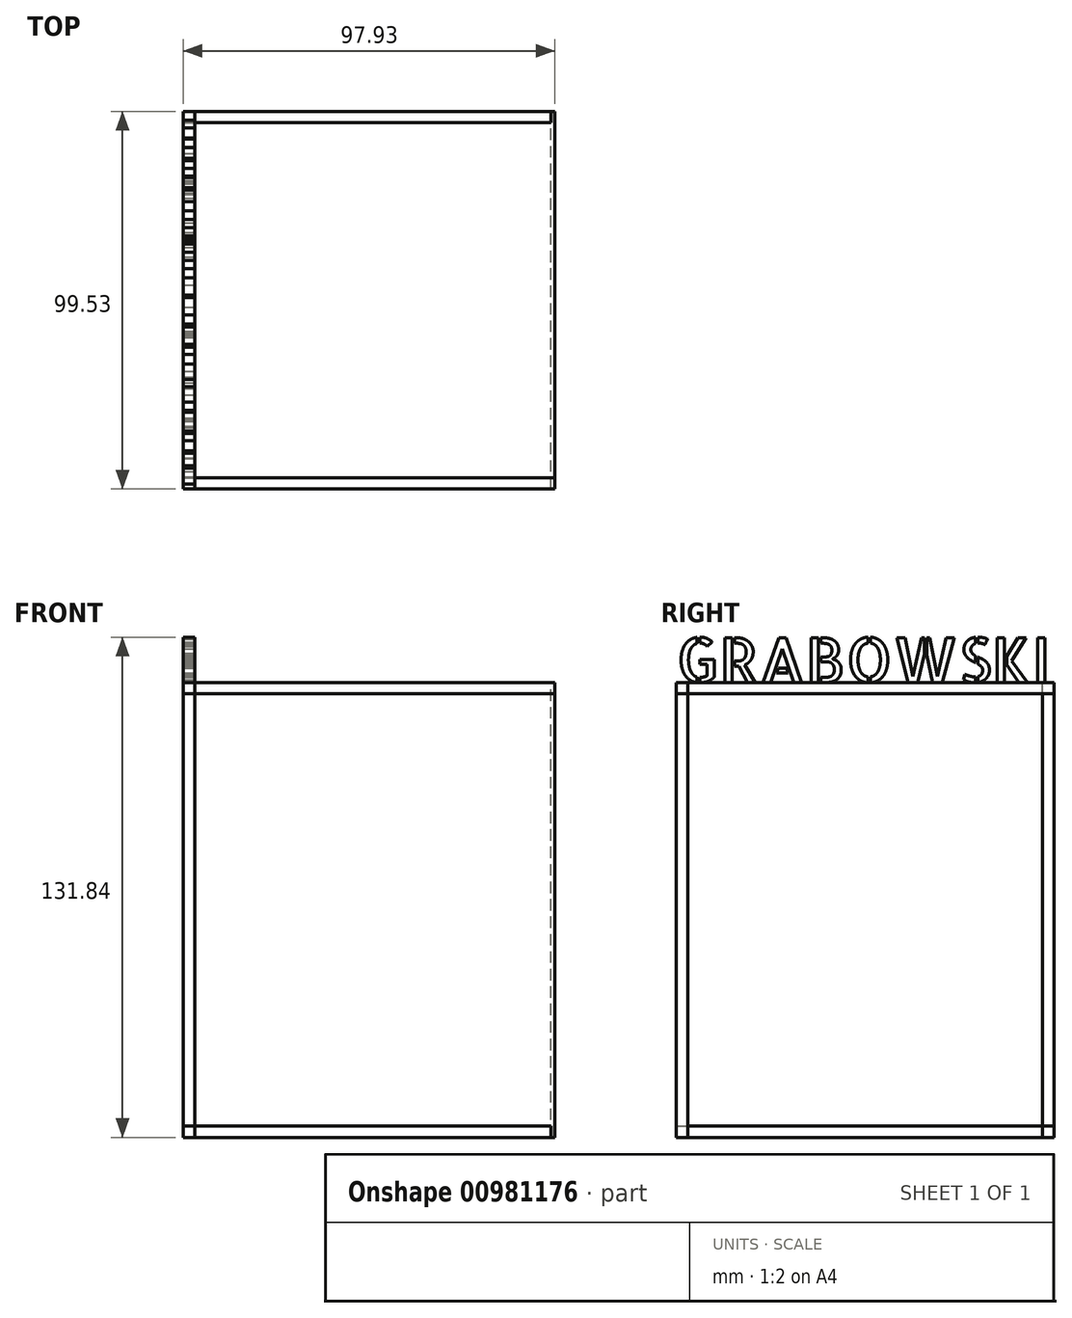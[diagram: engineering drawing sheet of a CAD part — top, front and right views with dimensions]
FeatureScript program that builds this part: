
annotation { "Feature Type Name" : "Feature", "Feature Type Description" : "" }
export const myFeature = defineFeature(function(context is Context, id is Id, definition is map)
    precondition{}
    {
        {
            var Q0;
            Q0=qCreatedBy(makeId("Front.planeOp"),FACE);
            var sketch = newSketch(context, id + "F0", { "sketchPlane" : qUnion([Q0])});
            skLineSegment(sketch, "E0.bottom", {"start": v(-41.77, 46.94) * mm, "end": v(56.16, 46.94) * mm});
            skLineSegment(sketch, "E0.top", {"start": v(-41.77, -72.94) * mm, "end": v(56.16, -72.94) * mm});
            skLineSegment(sketch, "E0.left", {"start": v(-41.77, 46.94) * mm, "end": v(-41.77, -72.94) * mm});
            skLineSegment(sketch, "E0.right", {"start": v(56.16, 46.94) * mm, "end": v(56.16, -72.94) * mm});
            skSolve(sketch);
        }
        {
            var Q0;
            Q0 = qSketchRegion(id + "F0", true);
            extrude(context, id + "F1", {"entities" : qUnion([Q0]), "depth" : 3 * mm, "offsetDistance" : 25 * mm});
        }
        {
            var Q0;
            Q0=makeQuery(id+"F1.opExtrude","SWEPT_FACE",FACE,{"disambiguationData":[OSD([sQuery(id+"F0.wireOp",EDGE,"E0.left")])]});
            var sketch = newSketch(context, id + "F2", { "sketchPlane" : qUnion([Q0])});
            skLineSegment(sketch, "E1.bottom", {"start": v(3, 46.94) * mm, "end": v(-96.53, 46.94) * mm});
            skLineSegment(sketch, "E1.top", {"start": v(3, -72.94) * mm, "end": v(-96.53, -72.94) * mm});
            skLineSegment(sketch, "E1.left", {"start": v(3, 46.94) * mm, "end": v(3, -72.94) * mm});
            skLineSegment(sketch, "E1.right", {"start": v(-96.53, 46.94) * mm, "end": v(-96.53, -72.94) * mm});
            skSolve(sketch);
        }
        {
            var Q0;
            {var subQ1=sQuery(id+"F0.wireOp",EDGE,"E0.left");var subQ2=makeQuery(id+"F1.opExtrude","CAP_EDGE",EDGE,{"disambiguationData":[OSD([subQ1])],"isStart":true});Q0=makeQuery(id+"F2.imprint","IMPRINT",FACE,{"disambiguationData":[TD([[makeQuery(id+"F2.imprint","IMPRINT",EDGE,{"derivedFrom":subQ2}),1.0]])]});}
            extrude(context, id + "F3", {"entities" : qUnion([Q0]), "operationType" : NewBodyOperationType.ADD, "oppositeDirection" : true, "depth" : 3 * mm, "offsetDistance" : 25 * mm});
        }
        {
            var Q0;
            Q0 = qSketchRegion(id + "F2", true);
            extrude(context, id + "F4", {"entities" : qUnion([Q0]), "oppositeDirection" : true, "depth" : 3 * mm, "offsetDistance" : 25 * mm});
        }
        {
            var Q0;
            Q0=makeQuery(id+"F4.opExtrude","SWEPT_FACE",FACE,{"disambiguationData":[OSD([sQuery(id+"F2.wireOp",EDGE,"E1.right")])]});
            var sketch = newSketch(context, id + "F5", { "sketchPlane" : qUnion([Q0])});
            skLineSegment(sketch, "E2.bottom", {"start": v(41.77, -72.94) * mm, "end": v(-55.1, -72.94) * mm});
            skLineSegment(sketch, "E2.top", {"start": v(41.77, 46.94) * mm, "end": v(-55.1, 46.94) * mm});
            skLineSegment(sketch, "E2.left", {"start": v(41.77, -72.94) * mm, "end": v(41.77, 46.94) * mm});
            skLineSegment(sketch, "E2.right", {"start": v(-55.1, -72.94) * mm, "end": v(-55.1, 46.94) * mm});
            skPoint(sketch, "E3.0", {"position": v(-56.16, -72.94) * mm});
            skSolve(sketch);
        }
        {
            var Q0;
            Q0 = qSketchRegion(id + "F5", true);
            extrude(context, id + "F6", {"entities" : qUnion([Q0]), "oppositeDirection" : true, "depth" : 3 * mm, "offsetDistance" : 25 * mm});
        }
        {
            var Q0;
            Q0=makeQuery(id+"F4.opExtrude","SWEPT_FACE",FACE,{"disambiguationData":[OSD([sQuery(id+"F2.wireOp",EDGE,"E1.top")])]});
            var sketch = newSketch(context, id + "F7", { "sketchPlane" : qUnion([Q0])});
            skLineSegment(sketch, "E4.bottom", {"start": v(-41.77, 3) * mm, "end": v(55.1, 3) * mm});
            skLineSegment(sketch, "E4.top", {"start": v(-41.77, -96.53) * mm, "end": v(55.1, -96.53) * mm});
            skLineSegment(sketch, "E4.left", {"start": v(-41.77, 3) * mm, "end": v(-41.77, -96.53) * mm});
            skLineSegment(sketch, "E4.right", {"start": v(55.1, 3) * mm, "end": v(55.1, -96.53) * mm});
            skSolve(sketch);
        }
        {
            var Q0;
            Q0 = qSketchRegion(id + "F7", true);
            extrude(context, id + "F8", {"entities" : qUnion([Q0]), "oppositeDirection" : true, "depth" : 3 * mm, "offsetDistance" : 25 * mm});
        }
        {
            var Q0;
            Q0=makeQuery(id+"F1.opExtrude","SWEPT_FACE",FACE,{"disambiguationData":[OSD([sQuery(id+"F0.wireOp",EDGE,"E0.bottom")])]});
            var sketch = newSketch(context, id + "F9", { "sketchPlane" : qUnion([Q0])});
            skPoint(sketch, "E5.0", {"position": v(-41.77, 96.53) * mm});
            skPoint(sketch, "E6.0", {"position": v(56.16, -3) * mm});
            skLineSegment(sketch, "E7.bottom", {"start": v(56.16, -3) * mm, "end": v(-41.77, -3) * mm});
            skLineSegment(sketch, "E7.top", {"start": v(56.16, 96.53) * mm, "end": v(-41.77, 96.53) * mm});
            skLineSegment(sketch, "E7.left", {"start": v(56.16, -3) * mm, "end": v(56.16, 96.53) * mm});
            skLineSegment(sketch, "E7.right", {"start": v(-41.77, -3) * mm, "end": v(-41.77, 96.53) * mm});
            skSolve(sketch);
        }
        {
            var Q0;
            Q0 = qSketchRegion(id + "F9", true);
            extrude(context, id + "F10", {"entities" : qUnion([Q0]), "oppositeDirection" : true, "depth" : 3 * mm, "offsetDistance" : 25 * mm});
        }
        {
            var Q0;
            Q0=makeQuery(id+"F4.opExtrude","CAP_FACE",FACE,{"disambiguationData":[OSD([sQuery(id+"F2.wireOp",EDGE,"E1.bottom"),sQuery(id+"F2.wireOp",EDGE,"E1.top"),sQuery(id+"F2.wireOp",EDGE,"E1.left"),sQuery(id+"F2.wireOp",EDGE,"E1.right")])],"isStart":false});
            var sketch = newSketch(context, id + "F11", { "sketchPlane" : qUnion([Q0])});
            skText(sketch, "E8", { "text": "GRABOWSKI", "fontName": "AllertaStencil-Regular.ttf"});
            const initialGuessF11  = {"E8": [-0.003, 0.04694, 1, 0, 0.01177]};
            skSetInitialGuess(sketch, initialGuessF11);
            skSolve(sketch);
        }
        {
            var Q0;
            Q0 = qSketchRegion(id + "F11", true);
            extrude(context, id + "F12", {"entities" : qUnion([Q0]), "oppositeDirection" : true, "depth" : 3 * mm, "offsetDistance" : 25 * mm});
        }
    });
